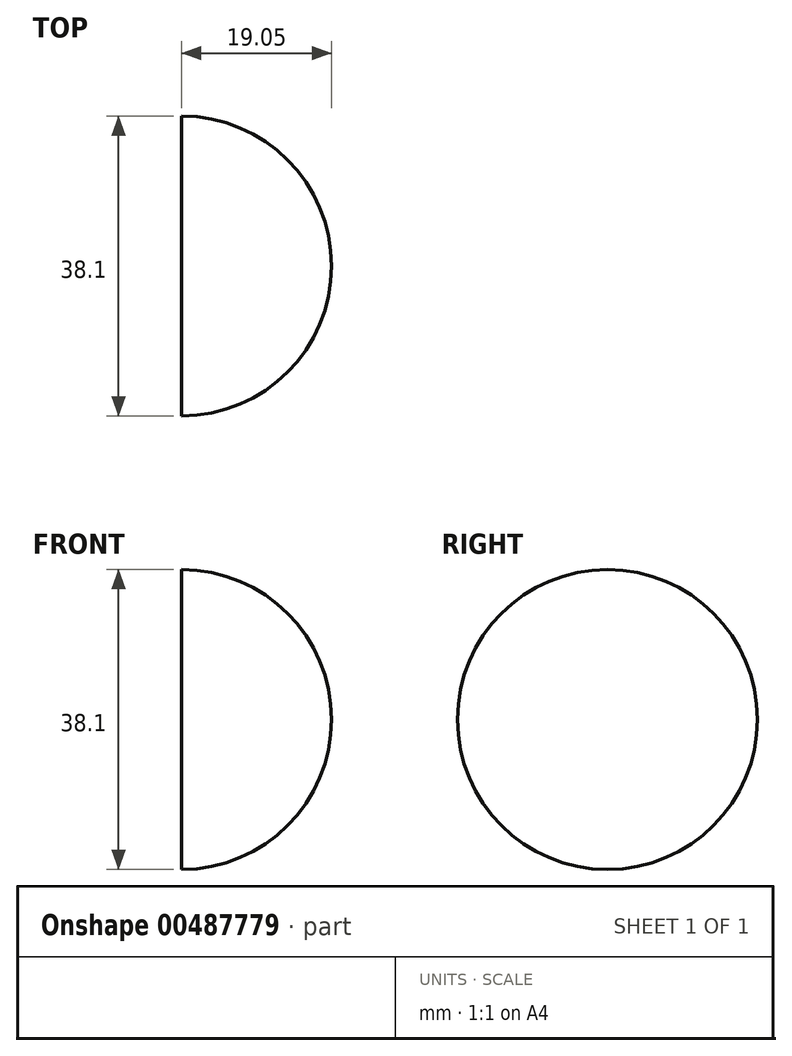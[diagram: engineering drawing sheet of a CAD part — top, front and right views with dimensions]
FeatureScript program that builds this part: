
annotation { "Feature Type Name" : "Feature", "Feature Type Description" : "" }
export const myFeature = defineFeature(function(context is Context, id is Id, definition is map)
    precondition{}
    {
        {
            var Q0;
            Q0=qCreatedBy(makeId("Right.planeOp"),FACE);
            var sketch = newSketch(context, id + "F0", { "sketchPlane" : qUnion([Q0])});
            skArc(sketch, "E0", {"start": v(0, -19.05) * mm, "mid": v(19.05, 0) * mm, "end": v(0, 19.05) * mm});
            skLineSegment(sketch, "E1", {"start": v(0, 19.05) * mm, "end": v(0, -19.05) * mm});
            skSolve(sketch);
        }
        {
            var Q0;
            {var subQ0=sQuery(id+"F0.wireOp",EDGE,"E1");Q0=makeQuery(id+"F0.imprint","IMPRINT",FACE,{"disambiguationData":[TD([[makeQuery(id+"F0.imprint","IMPRINT",EDGE,{"derivedFrom":subQ0}),1.0]])]});}
            var Q1;
            Q1=sQuery(id+"F0.wireOp",EDGE,"E1");
            revolve(context, id + "F1", {"entities" : qUnion([Q0]), "axis" : qUnion([Q1]), "revolveType" : RevolveType.ONE_DIRECTION, "angle" : 180 * degree});
        }
        {
            var Q0;
            Q0=makeQuery(id+"F1.opRevolve","CAP_FACE",FACE,{"disambiguationData":[OSD([sQuery(id+"F0.wireOp",EDGE,"E0"),sQuery(id+"F0.wireOp",EDGE,"E1")])],"isStart":true});
            shell(context, id + "F2", {"entities" : qUnion([Q0]), "thickness" : 0.03 * mm});
        }
    });
